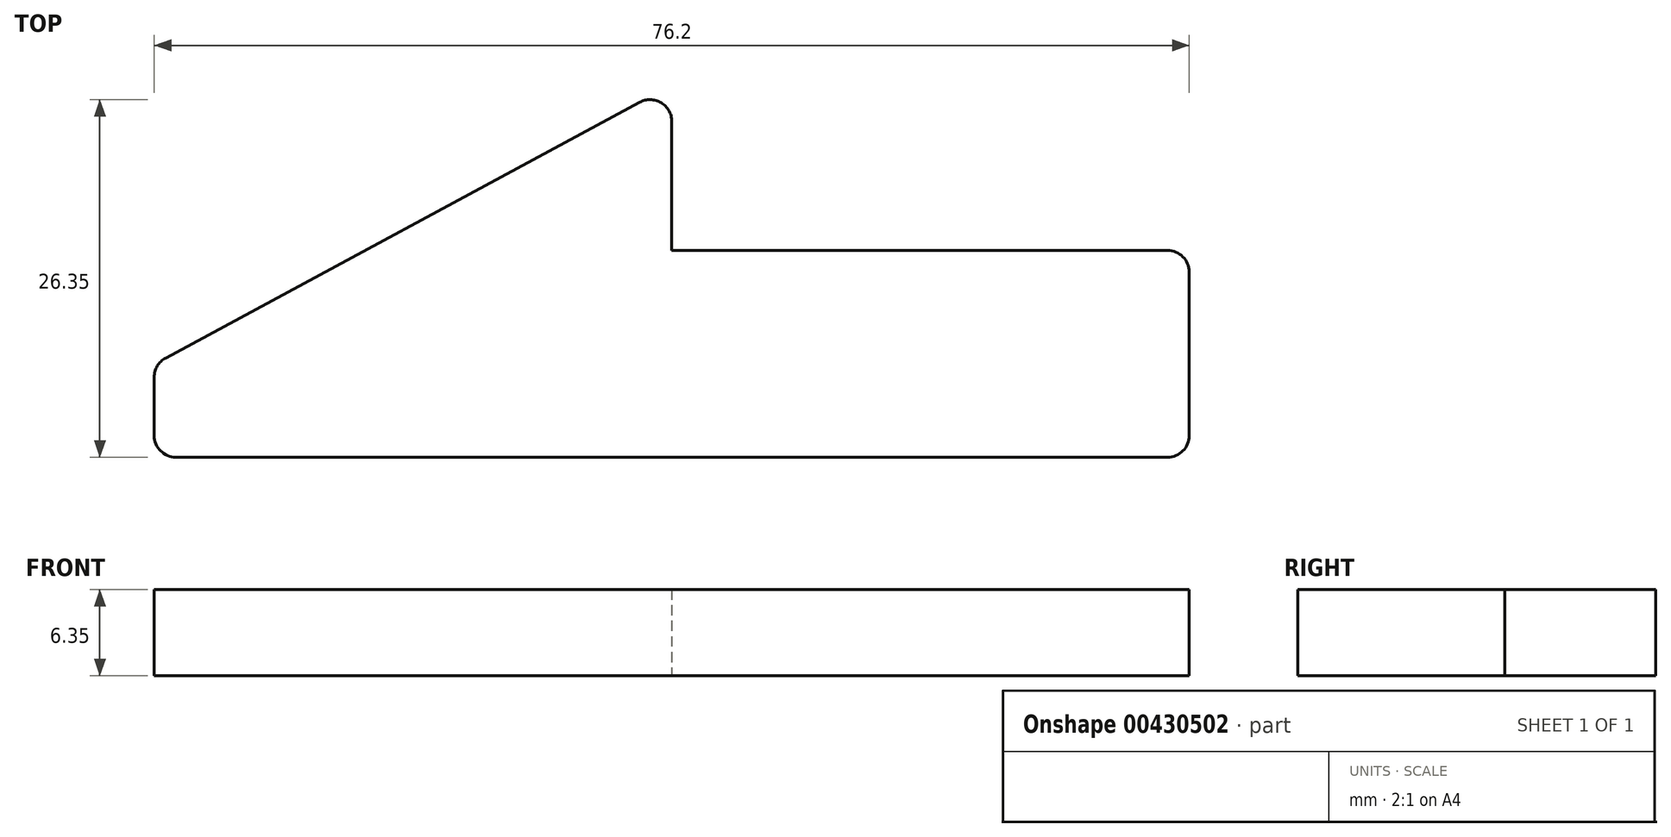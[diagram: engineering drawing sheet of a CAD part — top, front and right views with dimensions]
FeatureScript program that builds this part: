
annotation { "Feature Type Name" : "Feature", "Feature Type Description" : "" }
export const myFeature = defineFeature(function(context is Context, id is Id, definition is map)
    precondition{}
    {
        {
            var Q0;
            Q0=qCreatedBy(makeId("Top.planeOp"),FACE);
            var sketch = newSketch(context, id + "F0", { "sketchPlane" : qUnion([Q0])});
            skLineSegment(sketch, "E0", {"start": v(0, 0) * mm, "end": v(-60.58, 0) * mm});
            skLineSegment(sketch, "E1", {"start": v(-60.58, 0) * mm, "end": v(-60.58, 6.86) * mm});
            skLineSegment(sketch, "E2", {"start": v(-60.58, 6.86) * mm, "end": v(-22.48, 27.43) * mm});
            skLineSegment(sketch, "E3", {"start": v(-22.48, 27.43) * mm, "end": v(-22.48, 15.24) * mm});
            skLineSegment(sketch, "E4", {"start": v(-22.48, 15.24) * mm, "end": v(15.62, 15.24) * mm});
            skLineSegment(sketch, "E5", {"start": v(15.62, 15.24) * mm, "end": v(15.62, 0) * mm});
            skLineSegment(sketch, "E6", {"start": v(15.62, 0) * mm, "end": v(0, 0) * mm});
            skSolve(sketch);
        }
        {
            var Q0;
            Q0 = qSketchRegion(id + "F0", true);
            extrude(context, id + "F1", {"entities" : qUnion([Q0]), "depth" : 6.35 * mm});
        }
        {
            var Q0;
            Q0=makeQuery(id+"F1.opExtrude","SWEPT_EDGE",EDGE,{"disambiguationData":[OSD([sQuery(id+"F0.wireOp",EDGE,"E1"),sQuery(id+"F0.wireOp",EDGE,"E2")])]});
            var Q1;
            Q1=makeQuery(id+"F1.opExtrude","SWEPT_EDGE",EDGE,{"disambiguationData":[OSD([sQuery(id+"F0.wireOp",EDGE,"E0"),sQuery(id+"F0.wireOp",EDGE,"E1")])]});
            var Q2;
            Q2=makeQuery(id+"F1.opExtrude","SWEPT_EDGE",EDGE,{"disambiguationData":[OSD([sQuery(id+"F0.wireOp",EDGE,"E2"),sQuery(id+"F0.wireOp",EDGE,"E3")])]});
            var Q3;
            Q3=makeQuery(id+"F1.opExtrude","SWEPT_EDGE",EDGE,{"disambiguationData":[OSD([sQuery(id+"F0.wireOp",EDGE,"E4"),sQuery(id+"F0.wireOp",EDGE,"E5")])]});
            var Q4;
            Q4=makeQuery(id+"F1.opExtrude","SWEPT_EDGE",EDGE,{"disambiguationData":[OSD([sQuery(id+"F0.wireOp",EDGE,"E5"),sQuery(id+"F0.wireOp",EDGE,"E6")])]});
            fillet(context, id + "F2", {"entities" : qUnion([Q0, Q1, Q2, Q3, Q4]), "radius" : 1.6 * mm, "tangentPropagation" : true, "allowEdgeOverflow" : false});
        }
    });
